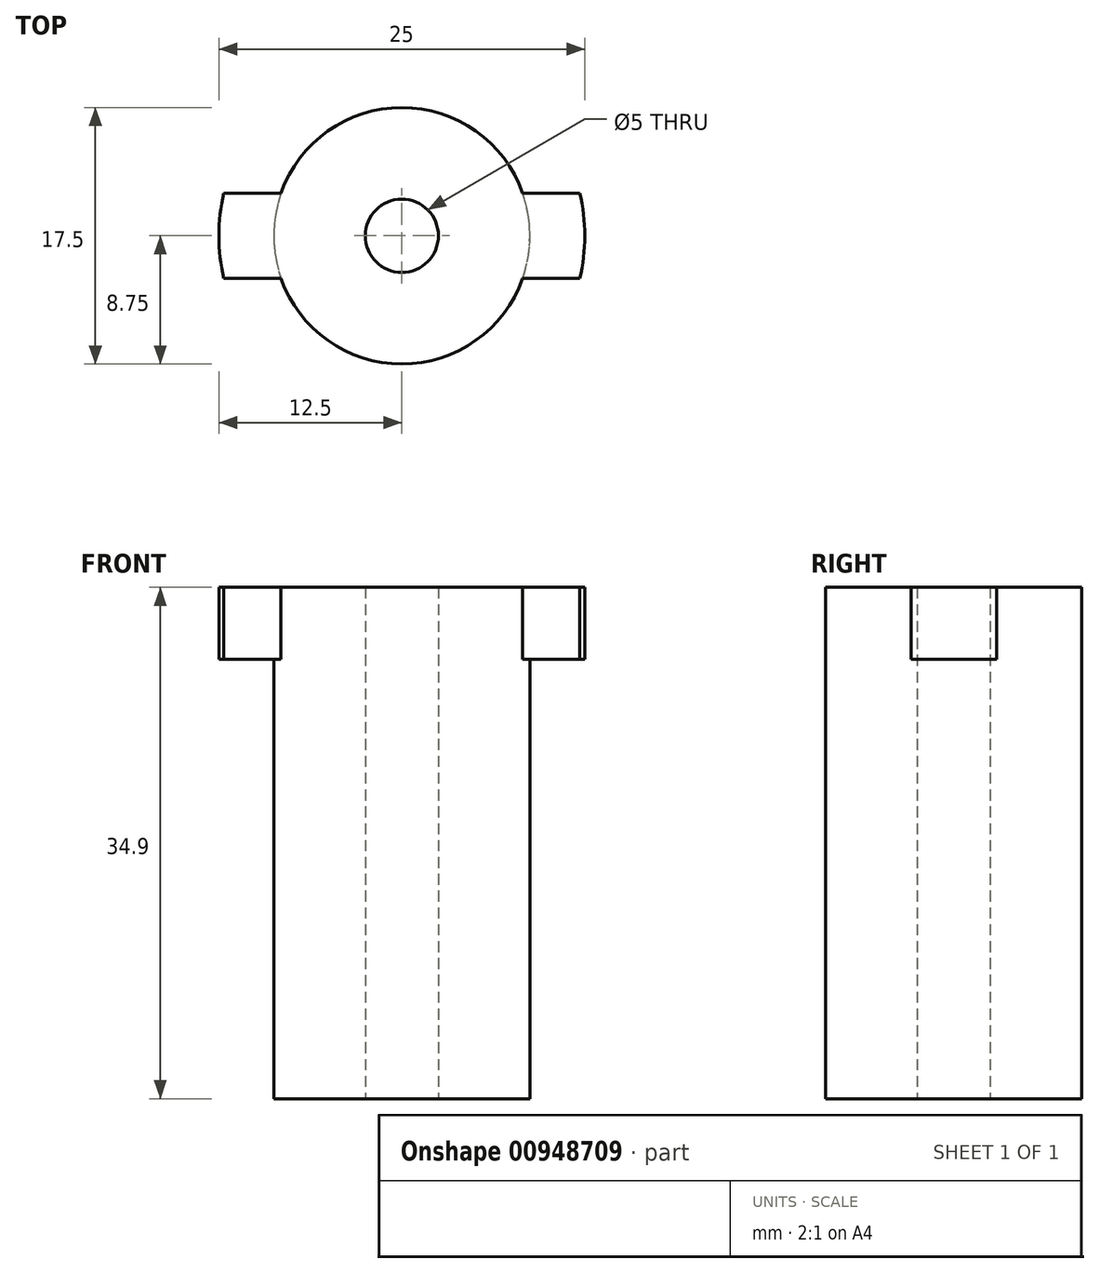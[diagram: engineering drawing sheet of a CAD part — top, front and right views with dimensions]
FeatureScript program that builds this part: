
annotation { "Feature Type Name" : "Feature", "Feature Type Description" : "" }
export const myFeature = defineFeature(function(context is Context, id is Id, definition is map)
    precondition{}
    {
        {
            var Q0;
            Q0=qCreatedBy(makeId("Top.planeOp"),FACE);
            var sketch = newSketch(context, id + "F0", { "sketchPlane" : qUnion([Q0])});
            skCircle(sketch, "E0", {"center": v(0, 0) * mm, "radius": 8.75 * mm});
            skSolve(sketch);
        }
        {
            var Q0;
            Q0=qSketchRegion(id+"F0",true);
            extrude(context, id + "F1", {"entities" : qUnion([Q0]), "depth" : 30 * mm, "offsetDistance" : 25 * mm});
        }
        {
            var Q0;
            Q0=makeQuery(id+"F1.opExtrude","CAP_FACE",FACE,{"disambiguationData":[OSD([sQuery(id+"F0.wireOp",EDGE,"E0")])],"isStart":false});
            var sketch = newSketch(context, id + "F2", { "sketchPlane" : qUnion([Q0])});
            skArc(sketch, "E1", {"start": v(-8.25, 2.92) * mm, "mid": v(0, 8.75) * mm, "end": v(8.25, 2.92) * mm});
            skArc(sketch, "E2", {"start": v(-8.25, -2.92) * mm, "mid": v(0, -8.75) * mm, "end": v(8.25, -2.92) * mm});
            skLineSegment(sketch, "E3", {"start": v(-8.25, 2.92) * mm, "end": v(-12.15, 2.92) * mm});
            skLineSegment(sketch, "E4", {"start": v(-8.25, -2.92) * mm, "end": v(-12.15, -2.92) * mm});
            skLineSegment(sketch, "E5", {"start": v(12.15, 2.92) * mm, "end": v(8.25, 2.92) * mm});
            skLineSegment(sketch, "E6", {"start": v(12.15, -2.92) * mm, "end": v(8.25, -2.92) * mm});
            skArc(sketch, "E7", {"start": v(-12.15, 2.92) * mm, "mid": v(-12.5, 0) * mm, "end": v(-12.15, -2.92) * mm});
            skArc(sketch, "E8", {"start": v(12.15, 2.92) * mm, "mid": v(12.5, 0) * mm, "end": v(12.15, -2.92) * mm});
            skSolve(sketch);
        }
        {
            var Q0;
            Q0=qSketchRegion(id+"F2",true);
            extrude(context, id + "F3", {"entities" : qUnion([Q0]), "operationType" : NewBodyOperationType.ADD, "depth" : (5 - 0.1) * mm, "offsetDistance" : 25 * mm});
        }
        {
            var Q0;
            Q0=makeQuery(id+"F1.opExtrude","CAP_FACE",FACE,{"disambiguationData":[OSD([sQuery(id+"F0.wireOp",EDGE,"E0")])],"isStart":true});
            var sketch = newSketch(context, id + "F4", { "sketchPlane" : qUnion([Q0])});
            skPoint(sketch, "E9", {"position": v(0, 0) * mm});
            skSolve(sketch);
        }
        {
            var Q0;
            Q0=sQuery(id+"F4.wireOp",VERTEX,"E9");
            var Q1;
            Q1=makeQuery(id+"F1.opExtrude","SWEPT_BODY",BODY,{"disambiguationData":[OSD([sQuery(id+"F0.wireOp",EDGE,"E0")])]});
            hole(context, id + "F5", {"style" : HoleStyle.SIMPLE, "endStyle" : HoleEndStyle.THROUGH, "holeDiameter" : 5 * mm, "majorDiameter" : 5 * mm, "isTappedThrough" : true, "tappedDepth" : 12 * mm, "tapClearance" : 3, "locations" : qUnion([Q0]), "scope" : qUnion([Q1])});
        }
    });
